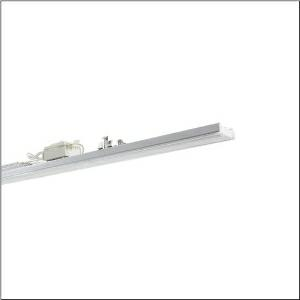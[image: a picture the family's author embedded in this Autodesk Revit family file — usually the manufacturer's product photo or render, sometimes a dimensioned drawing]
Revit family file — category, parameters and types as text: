
# Revit family: licross_r__11_recessed_mo_51tl12dn4axg3s4_5beb
name_source: partatom
category: Lighting Fixtures
units: mm (PartAtom-declared; Revit-internal decimal feet)

## family parameters
Cut with Voids When Loaded = No
Host = Face
Light Source = No
Part Type = Normal
Room Calculation Point = No
Round Connector Dimension = Use Diameter
Shared = No

## types (1)
- --- (1 x LED, 1010 lm, 6.7 W, 4000K)
    Apparent Load = 7 VA
    CIE Flux Codes = 67 92 99 100 100
    Color Rendering = 80
    Color Temperature = 4000K
    Default Elevation = 1800 mm
    Description = Licross® 11 Recessed MO, luminaire insert, of sheet steel, coil coated, white, length: 1.500mm, width: 66mm, height: 67mm, LED rated luminous flux: 10.240lm, light colour: 840, control gear: DALI 2, with plug, 6-pole, with phase selection, for trunking rail, 9 or 11-core, mains connection: 220..240V, AC, 50/60Hz, rated input power: 61W, for trunking rail, 9-/11-core, internal wiring halogen-free, for emergency light function, converter,control gear: single battery element, battery: LiFePO4, 9Ah, primary optical cover: cover, of PMMA, light emission: direct distribution, primary light characteristic: symmetric, protection rating (complete): IP40, insulation class (complete): insulation class I (protective earthing), certification: CE, UKCA, protection symbol: D if used in an environment without relevant dust loads with corresponding accessories, impact resistance: IK06, permissible ambient temperature for indoor applications: +5..+35°C, standard: EN 60598-2-22, LABS conformity tested according to VDMA 24364:2018-05, reducing of maximum allowable ambient temperature of 5°C with ceiling mounting, corresponds to IFS (International Featured Standards) requirements for safety and quality in the food industry, packaging unit: 1 piece
    Height = 58 mm
    Lamp = 1 x LED
    Lamp Light Flux = 1010 lm
    Lamp Power = 6.7 W
    Lamp count = 1
    Length = 1500 mm
    Luminous efficacy = 151 lm/W
    Manufacturer = Siteco
    ModVariant = No
    Model = 51TL12DN4AXG3S4
    Mounting Place = Ceiling
    Mounting Type = Pendant
    Number of Poles = 1
    OnlyDefault = Yes
    Power Factor = 1
    Product Name = Licross® 11 Recessed MO
    Product group = luminaire insert | ceiling pendant
    ProductGroupID = 902
    Protection Class = Protection class I
    Protection Degree = IP 40
    RLX_Detail_Level = 1
    RLX_Emergency_Light_Flux = 0 lm
    RLX_Emergency_Type = 0
    RLX_Emergency_Type_DB = No
    RlxData = <blob elided: 24817 chars, md5=976bb691>
    Socket = socket
    Standby Power = 0 W
    System Light Flux = 1010 lm
    System Power = 7 W
    Type Comments = : emergency light operation: 3 h
    Type Image = l_1296930.jpg
    URL = http://relux.com
    VarID = @adj_111683
    Voltage = 0 V
    Weight = 0.00 kg
    Width = 66 mm

## geometry (parser evidence)
native form markers: Blend x4, Sweep x11
no freeform markers — native parametric forms only
